# Revit family: O29211001_Sanitario Smart Redondo
name_source: partatom
category: Plumbing Fixtures
units: mm (PartAtom-declared; Revit-internal decimal feet)

## family parameters
Always vertical = Yes
Cut with Voids When Loaded = No
Host = Wall
OmniClass Number = 23.31.19.17
OmniClass Title = Toilets With Tank
Part Type = Normal
Room Calculation Point = No
Round Connector Dimension = Use Diameter
Shared = No

## types (1)
- Type 1
    Alto = 629 mm  [stored 2.06365 ft]
    Altura de sello = 61 mm - 2.4 pulg
    Ancho = 368 mm  [stored 1.20735 ft]
    Creado por = BIMBAU
    Default Elevation = 0 mm  [stored 0 ft]
    Diámetro del sifón = 50.8 mm - 2 pulg
    Espejo de agua = 181 x 241 mm - 7.1 x 9.1 pulg
    Fecha de creación = 15/03/2021
    Manufacturer = Corona
    Material = Corona_Plastico_Blanco
    Material 2 = Corona_Plastico_Blanco
    Material 3 = Corona_Plastico_Cromado
    Model = Sanitario Smart Redondo de una pieza
    Peso Bruto aprox = 31.1 kg - 68.5 lb
    Peso Neto aprox = 29.5 kg - 65 lb
    Presion maxima = 20 - 80 PSI
    Profundidad = 690 mm  [stored 2.26378 ft]
    Referencia = O29211001
    Sistema de descarga = Variable - Por gravedad
    URL = https://corona.co

note: [stored X ft] marks values corroborated as IEEE doubles in the binary element streams (Revit-internal decimal feet)

## geometry (parser evidence)
native form markers: Sweep x7
no freeform markers — native parametric forms only
